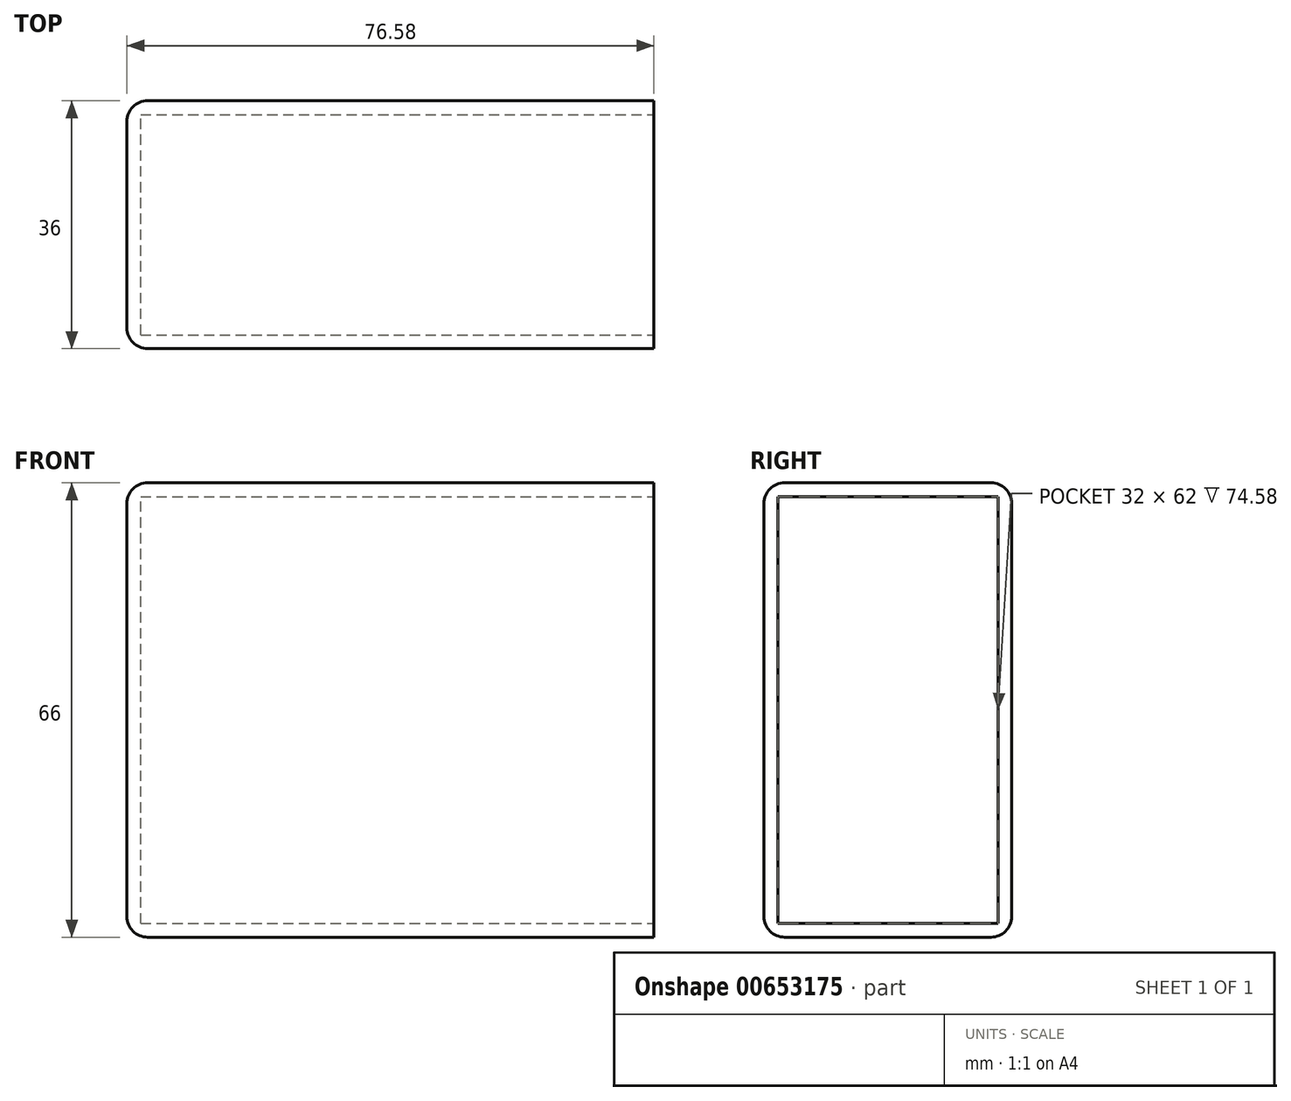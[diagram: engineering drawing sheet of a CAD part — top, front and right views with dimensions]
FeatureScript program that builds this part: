
annotation { "Feature Type Name" : "Feature", "Feature Type Description" : "" }
export const myFeature = defineFeature(function(context is Context, id is Id, definition is map)
    precondition{}
    {
        {
            var Q0;
            Q0=qCreatedBy(makeId("Front.planeOp"),FACE);
            var sketch = newSketch(context, id + "F0", { "sketchPlane" : qUnion([Q0])});
            skLineSegment(sketch, "E0.bottom", {"start": v(0, 0) * mm, "end": v(76.58, 0) * mm});
            skLineSegment(sketch, "E0.top", {"start": v(0, 66) * mm, "end": v(76.58, 66) * mm});
            skLineSegment(sketch, "E0.left", {"start": v(0, 0) * mm, "end": v(0, 66) * mm});
            skLineSegment(sketch, "E0.right", {"start": v(76.58, 0) * mm, "end": v(76.58, 66) * mm});
            skSolve(sketch);
        }
        {
            var Q0;
            Q0=makeQuery(id+"F0.imprint","IMPRINT",FACE,{"disambiguationData":[TD([[makeQuery(id+"F0.imprint","IMPRINT",EDGE,{"derivedFrom":sQuery(id+"F0.wireOp",EDGE,"E0.bottom")}),1.0]])]});
            extrude(context, id + "F1", {"entities" : qUnion([Q0]), "depth" : 36 * mm, "offsetDistance" : 25.4 * mm});
        }
        {
            var Q0;
            Q0=makeQuery(id+"F1.opExtrude","SWEPT_FACE",FACE,{"disambiguationData":[OSD([sQuery(id+"F0.wireOp",EDGE,"E0.right")])]});
            shell(context, id + "F2", {"entities" : qUnion([Q0]), "thickness" : 2 * mm});
        }
        {
            var Q0;
            Q0=makeQuery(id+"F1.opExtrude","CAP_EDGE",EDGE,{"disambiguationData":[OSD([sQuery(id+"F0.wireOp",EDGE,"E0.bottom")])],"isStart":true});
            var Q1;
            Q1=makeQuery(id+"F1.opExtrude","CAP_EDGE",EDGE,{"disambiguationData":[OSD([sQuery(id+"F0.wireOp",EDGE,"E0.bottom")])],"isStart":false});
            var Q2;
            Q2=makeQuery(id+"F1.opExtrude","CAP_EDGE",EDGE,{"disambiguationData":[OSD([sQuery(id+"F0.wireOp",EDGE,"E0.top")])],"isStart":true});
            var Q3;
            Q3=makeQuery(id+"F1.opExtrude","CAP_EDGE",EDGE,{"disambiguationData":[OSD([sQuery(id+"F0.wireOp",EDGE,"E0.top")])],"isStart":false});
            fillet(context, id + "F3", {"entities" : qUnion([Q0, Q1, Q2, Q3]), "radius" : 3 * mm, "tangentPropagation" : true, "allowEdgeOverflow" : false});
        }
        {
            var Q0;
            Q0=makeQuery(id+"F1.opExtrude","SWEPT_EDGE",EDGE,{"disambiguationData":[OSD([sQuery(id+"F0.wireOp",EDGE,"E0.top"),sQuery(id+"F0.wireOp",EDGE,"E0.left")])]});
            fillet(context, id + "F4", {"entities" : qUnion([Q0]), "radius" : 3 * mm, "tangentPropagation" : true, "allowEdgeOverflow" : false});
        }
    });
